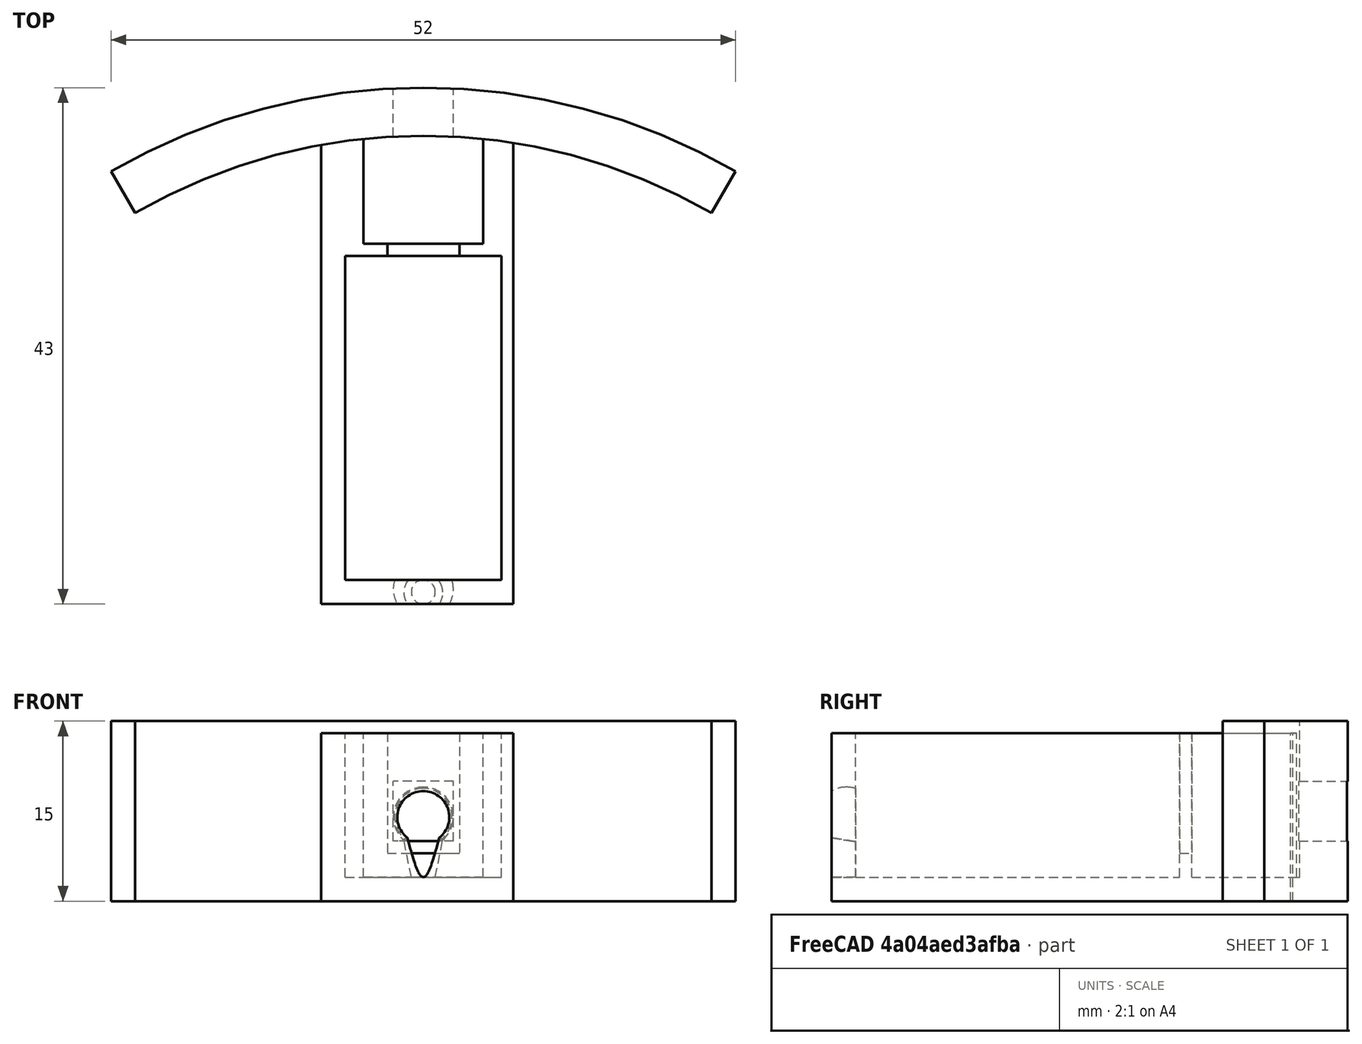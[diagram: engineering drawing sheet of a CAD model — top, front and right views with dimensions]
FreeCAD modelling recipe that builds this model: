
FCSTD DOCUMENT  (FreeCAD 0.16R4924 (Git))
Label: solenoid_bay_v2_with_wall
License: All rights reserved
LicenseURL: http://en.wikipedia.org/wiki/All_rights_reserved
objects: Part::Cut×7, Part::Box×5, Part::Cylinder×2, Part::Sphere×1, Part::Cone×1, Part::MultiFuse×1
note: 17 computed .brp shape members not serialized (recipe doc carries the construction recipe); baked Part::Feature solids carry a one-line shape summary decoded from their .brp

FEATURE [Part::Box] Box  label="Case"
  Height = 14
  Length = 16
  Width = 40
FEATURE [Part::Box] Box001  label="solenoidBay"
  Height = 12
  Length = 13
  Placement = pos=(2,2,2) rot=(0,0,1;0rad)
  Width = 27
FEATURE [Part::Cut] Cut
  Base = -> Box
  Tool = -> Box001
FEATURE [Part::Box] Box002  label="pullBay"
  Height = 15
  Length = 10
  Placement = pos=(3.5,30,2) rot=(0,0,1;0rad)
  Width = 10
FEATURE [Part::Cut] Cut001
  Base = -> Cut
  Tool = -> Box002
FEATURE [Part::Box] Box003  label="neck"
  Height = 15
  Length = 6
  Placement = pos=(5.5,28,4) rot=(0,0,1;0rad)
  Width = 4
FEATURE [Part::Cut] Cut002
  Base = -> Cut001
  Tool = -> Box003
FEATURE [Part::Sphere] Sphere  label="pinhole"
  Angle1 = -90
  Angle2 = 90
  Angle3 = 360
  Placement = pos=(8.5,1.25,7) rot=(0,0,1;0rad)
  Radius = 2.5
FEATURE [Part::Cut] Cut003
  Base = -> Cut002
  Tool = -> Sphere
FEATURE [Part::Cone] Cone
  Angle = 360
  Height = 5
  Placement = pos=(8.5,1,2) rot=(0,0,1;0rad)
  Radius1 = 1
  Radius2 = 2
FEATURE [Part::Cut] Cut004
  Base = -> Cut003
  Tool = -> Cone
FEATURE [Part::Cylinder] Cylinder  label="bottle_wall"
  Angle = 60
  Height = 15
  Placement = pos=(8.5,-7,0) rot=(0,0,1;1.0472rad)
  Radius = 52
FEATURE [Part::Cylinder] Cylinder001  label="bottle_wall001"
  Angle = 60
  Height = 15
  Placement = pos=(8.5,-7,0) rot=(0,0,1;1.0472rad)
  Radius = 48
FEATURE [Part::Cut] Cut005
  Base = -> Cylinder
  Placement = pos=(0,-2,0) rot=(0,0,1;0rad)
  Tool = -> Cylinder001
FEATURE [Part::MultiFuse] Fusion
  Shapes = -> [Cut004,Cut005]
FEATURE [Part::Box] Box004  label="pin_opening"
  Height = 5
  Length = 5
  Placement = pos=(6,38.5,5) rot=(0,0,1;0rad)
  Width = 5
FEATURE [Part::Cut] Cut006
  Base = -> Fusion
  Tool = -> Box004
